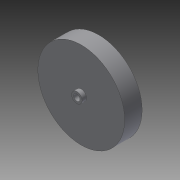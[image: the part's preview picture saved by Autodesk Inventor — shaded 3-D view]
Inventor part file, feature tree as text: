
AUTODESK INVENTOR PART (.ipt)
format: ipt  version: 2014 SP1 (Build 180222100, 222)  size: 83,968 bytes
history: native  units: in
note: dims shown in document units (in); Inventor stores cm internally (conversion verified against a paired STEP export)
features: extrude x2, sketch x1
ambient origin geometry x8: Origin, YZ Plane, XZ Plane, XY Plane, X Axis, Y Axis, Z Axis, Center Point
bodies: Solid1 (feature_tree)
feature tree (3):
  sketch  "Sketch1"  dims[d0=4.125in d1=0.3in d2=0.5in d3=0.83in d4=0.0in d5=1.25in d6=0.0in]
  extrude  "Extrusion1"  Depth=1.25in
  extrude  "Extrusion2"  Depth=1.25in
